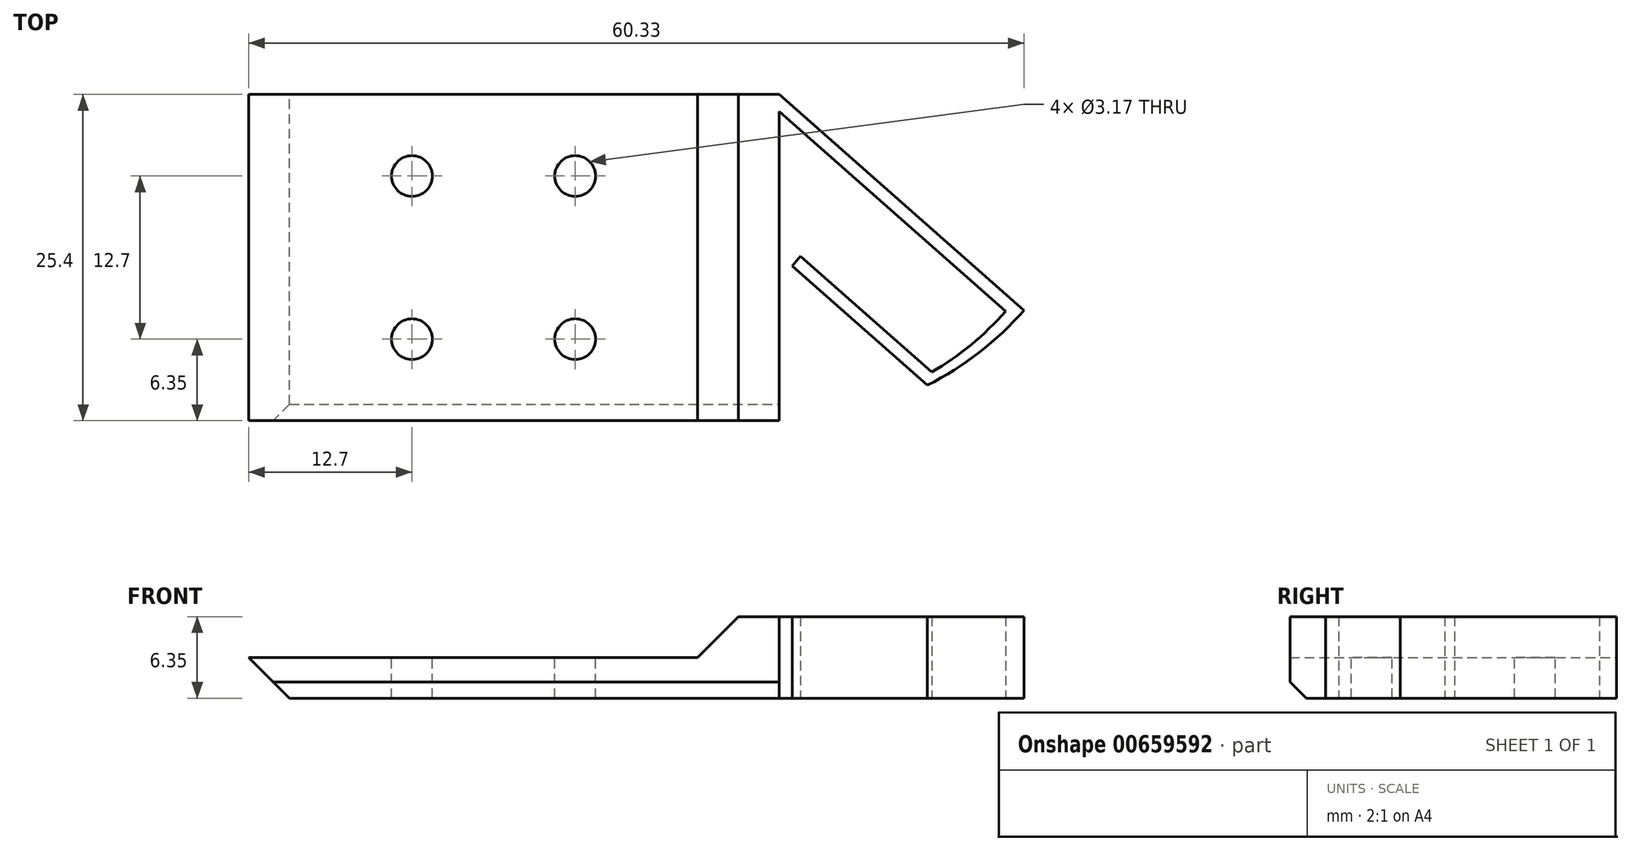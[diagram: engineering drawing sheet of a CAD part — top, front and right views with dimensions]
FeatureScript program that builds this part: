
annotation { "Feature Type Name" : "Feature", "Feature Type Description" : "" }
export const myFeature = defineFeature(function(context is Context, id is Id, definition is map)
    precondition{}
    {
        {
            var Q0;
            Q0=qCreatedBy(makeId("Top.planeOp"),FACE);
            var sketch = newSketch(context, id + "F0", { "sketchPlane" : qUnion([Q0])});
            skLineSegment(sketch, "E0.bottom", {"start": v(28.58, -12.7) * mm, "end": v(-28.58, -12.7) * mm});
            skLineSegment(sketch, "E0.top", {"start": v(28.58, 12.7) * mm, "end": v(-28.58, 12.7) * mm});
            skLineSegment(sketch, "E0.left", {"start": v(28.58, -12.7) * mm, "end": v(28.58, 12.7) * mm});
            skLineSegment(sketch, "E0.right", {"start": v(-28.57, -12.7) * mm, "end": v(-28.57, 12.7) * mm});
            skPoint(sketch, "E0.middle", {"position": v(0, 0) * mm});
            skLineSegment(sketch, "E1", {"start": v(-9.53, 11.37) * mm, "end": v(-9.52, -12.7) * mm});
            skLineSegment(sketch, "E2", {"start": v(0, -12.7) * mm, "end": v(0, 12.7) * mm});
            skPoint(sketch, "E3", {"position": v(-22.22, -12.7) * mm});
            skLineSegment(sketch, "E4", {"start": v(-9.53, 12.7) * mm, "end": v(-28.57, -4.1) * mm});
            skPoint(sketch, "E5", {"position": v(-19.05, -12.7) * mm});
            skArc(sketch, "E6", {"start": v(-28.57, -4.1) * mm, "mid": v(-25.09, -7.37) * mm, "end": v(-21.05, -9.94) * mm});
            skLineSegment(sketch, "E7", {"start": v(-21.05, -9.94) * mm, "end": v(-10.53, -0.66) * mm});
            skLineSegment(sketch, "E8", {"start": v(-10.53, -0.66) * mm, "end": v(-11.19, 0.1) * mm});
            skLineSegment(sketch, "E9", {"start": v(-11.19, 0.1) * mm, "end": v(-11.19, 0.1) * mm});
            skLineSegment(sketch, "E10", {"start": v(-9.53, 11.37) * mm, "end": v(-27.15, -4.18) * mm});
            skArc(sketch, "E11", {"start": v(-27.15, -4.18) * mm, "mid": v(-24.46, -6.77) * mm, "end": v(-21.4, -8.91) * mm});
            skLineSegment(sketch, "E12", {"start": v(-21.4, -8.91) * mm, "end": v(-11.19, 0.1) * mm});
            skSolve(sketch);
        }
        {
            var Q0;
            {var subQ0=sQuery(id+"F0.wireOp",EDGE,"E0.left");Q0=makeQuery(id+"F0.imprint","IMPRINT",FACE,{"disambiguationData":[TD([[makeQuery(id+"F0.imprint","IMPRINT",EDGE,{"derivedFrom":subQ0}),1.0]])]});}
            var Q1;
            {var subQ1=sQuery(id+"F0.wireOp",EDGE,"E1");Q1=makeQuery(id+"F0.imprint","IMPRINT",FACE,{"disambiguationData":[TD([[makeQuery(id+"F0.imprint","IMPRINT",EDGE,{"derivedFrom":subQ1}),1.0]])]});}
            var Q2;
            {var subQ0=sQuery(id+"F0.wireOp",EDGE,"Ll8NUgnO-918t-zldm-zNWz-RsUZQomu35K8");Q2=makeQuery(id+"F0.imprint","IMPRINT",FACE,{"disambiguationData":[TD([[makeQuery(id+"F0.imprint","IMPRINT",EDGE,{"derivedFrom":subQ0}),1.0]])]});}
            extrude(context, id + "F1", {"entities" : qUnion([Q0, Q1, Q2]), "depth" : 3.17 * mm, "offsetDistance" : 25.4 * mm});
        }
        {
            var Q0;
            {var subQ1=sQuery(id+"F0.wireOp",EDGE,"E1");Q0=makeQuery(id+"F0.imprint","IMPRINT",FACE,{"disambiguationData":[TD([[makeQuery(id+"F0.imprint","IMPRINT",EDGE,{"derivedFrom":subQ1}),1.0]])]});}
            extrude(context, id + "F2", {"entities" : qUnion([Q0]), "operationType" : NewBodyOperationType.ADD, "depth" : 6.35 * mm, "offsetDistance" : 25.4 * mm});
        }
        {
            var Q0;
            Q0=makeQuery(id+"F2.opExtrude","CAP_EDGE",EDGE,{"disambiguationData":[OSD([sQuery(id+"F0.wireOp",EDGE,"E2")])],"isStart":false});
            chamfer(context, id + "F3", {"entities" : qUnion([Q0]), "width" : 6.35 * mm, "tangentPropagation" : true});
        }
        {
            var Q0;
            {var subQ0=sQuery(id+"F0.wireOp",EDGE,"E0.left");Q0=makeQuery(id+"F37SAEC6IVc2ddh_1.boolean.opBoolean","MERGE",FACE,{"derivedFrom":[makeQuery(id+"F1.opExtrude","SWEPT_FACE",FACE,{"disambiguationData":[OSD([subQ0])]}),makeQuery(id+"F37SAEC6IVc2ddh_1.opExtrude","SWEPT_FACE",FACE,{"disambiguationData":[OSD([subQ0])]})]});}
            cPlane(context, id + "F4", {"entities" : qUnion([Q0]), "cplaneType" : CPlaneType.OFFSET, "offset" : 3.17 * mm, "width" : 152.4 * mm, "height" : 152.4 * mm});
        }
        {
            var Q0;
            {var subQ0=sQuery(id+"F0.wireOp",EDGE,"E1");Q0=makeQuery(id+"F2.boolean.opBoolean","MERGE",FACE,{"derivedFrom":[makeQuery(id+"F1.opExtrude","SWEPT_FACE",FACE,{"disambiguationData":[OSD([subQ0])]}),makeQuery(id+"F2.opExtrude","SWEPT_FACE",FACE,{"disambiguationData":[OSD([subQ0])]})]});}
            var sketch = newSketch(context, id + "F5", { "sketchPlane" : qUnion([Q0])});
            skLineSegment(sketch, "E13", {"start": v(12.7, 0) * mm, "end": v(12.7, 1.27) * mm});
            skLineSegment(sketch, "E14", {"start": v(12.7, 1.27) * mm, "end": v(11.43, 0) * mm});
            skLineSegment(sketch, "E15", {"start": v(11.43, 0) * mm, "end": v(12.7, 0) * mm});
            skSolve(sketch);
        }
        {
            var Q0;
            {var subQ0=sQuery(id+"F0.wireOp",EDGE,"E0.top");Q0=makeQuery(id+"F2.boolean.opBoolean","MERGE",FACE,{"derivedFrom":[makeQuery(id+"F1.opExtrude","SWEPT_FACE",FACE,{"disambiguationData":[OSD([subQ0])]}),makeQuery(id+"F2.opExtrude","SWEPT_FACE",FACE,{"disambiguationData":[OSD([subQ0])]})]});}
            var sketch = newSketch(context, id + "F6", { "sketchPlane" : qUnion([Q0])});
            skLineSegment(sketch, "E16", {"start": v(-28.58, 3.18) * mm, "end": v(-31.75, 3.18) * mm});
            skLineSegment(sketch, "E17", {"start": v(-31.75, 3.18) * mm, "end": v(-28.58, 0) * mm});
            skLineSegment(sketch, "E18", {"start": v(-28.58, 0) * mm, "end": v(-28.58, 3.18) * mm});
            skSolve(sketch);
        }
        {
            var Q0;
            Q0=makeQuery(id+"F6.imprint","IMPRINT",FACE,{"disambiguationData":[TD([[makeQuery(id+"F6.imprint","IMPRINT",EDGE,{"derivedFrom":sQuery(id+"F6.wireOp",EDGE,"E18")}),1.0]])]});
            var Q1;
            Q1=makeQuery(id+"F6.imprint","IMPRINT",FACE,{"disambiguationData":[TD([[makeQuery(id+"F6.imprint","IMPRINT",EDGE,{"derivedFrom":sQuery(id+"F6.wireOp",EDGE,"E16")}),1.0]])]});
            extrude(context, id + "F7", {"entities" : qUnion([Q0, Q1]), "operationType" : NewBodyOperationType.ADD, "oppositeDirection" : true, "depth" : 25.4 * mm, "offsetDistance" : 25.4 * mm});
        }
        {
            var Q0;
            Q0=makeQuery(id+"F5.imprint","IMPRINT",FACE,{"disambiguationData":[TD([[makeQuery(id+"F5.imprint","IMPRINT",EDGE,{"derivedFrom":sQuery(id+"F5.wireOp",EDGE,"E13")}),-1.0]])]});
            extrude(context, id + "F8", {"entities" : qUnion([Q0]), "operationType" : NewBodyOperationType.REMOVE, "oppositeDirection" : true, "depth" : 50.8 * mm, "offsetDistance" : 25.4 * mm});
        }
        {
            var Q0;
            Q0=makeQuery(id+"F1.opExtrude","SWEPT_BODY",BODY,{"disambiguationData":[OSD([sQuery(id+"F0.wireOp",EDGE,"E0.bottom"),sQuery(id+"F0.wireOp",EDGE,"E0.top"),sQuery(id+"F0.wireOp",EDGE,"E0.left"),sQuery(id+"F0.wireOp",EDGE,"E1"),sQuery(id+"F0.wireOp",EDGE,"E4"),sQuery(id+"F0.wireOp",EDGE,"E6"),sQuery(id+"F0.wireOp",EDGE,"E7"),sQuery(id+"F0.wireOp",EDGE,"E8"),sQuery(id+"F0.wireOp",EDGE,"E10"),sQuery(id+"F0.wireOp",EDGE,"E11"),sQuery(id+"F0.wireOp",EDGE,"E12")])]});
            var Q1;
            Q1=qCreatedBy(id+"F4.planeOp",FACE);
            mirror(context, id + "F9", {"entities" : qUnion([Q0]), "mirrorPlane" : qUnion([Q1])});
        }
        {
            var Q0;
            {var subQ0=sQuery(id+"F0.wireOp",EDGE,"E0.top");Q0=makeQuery(id+"F7.boolean.opBoolean","MERGE",FACE,{"derivedFrom":[makeQuery(id+"F1.opExtrude","CAP_FACE",FACE,{"disambiguationData":[OSD([sQuery(id+"F0.wireOp",EDGE,"E0.bottom"),subQ0,sQuery(id+"F0.wireOp",EDGE,"E0.left"),sQuery(id+"F0.wireOp",EDGE,"E1"),sQuery(id+"F0.wireOp",EDGE,"E4"),sQuery(id+"F0.wireOp",EDGE,"E6"),sQuery(id+"F0.wireOp",EDGE,"E7"),sQuery(id+"F0.wireOp",EDGE,"E8"),sQuery(id+"F0.wireOp",EDGE,"E10"),sQuery(id+"F0.wireOp",EDGE,"E11"),sQuery(id+"F0.wireOp",EDGE,"E12")])],"isStart":false}),makeQuery(id+"F7.opExtrude","SWEPT_FACE",FACE,{"disambiguationData":[OSD([subQ0,sQuery(id+"F6.wireOp",EDGE,"E16")])]})]});}
            var sketch = newSketch(context, id + "F10", { "sketchPlane" : qUnion([Q0])});
            skLineSegment(sketch, "E19", {"start": v(31.75, 0) * mm, "end": v(19.05, 0) * mm, "construction": true});
            skPoint(sketch, "E19.endSnap0", {"position": v(-3.17, 0) * mm});
            skLineSegment(sketch, "E20", {"start": v(19.05, 0) * mm, "end": v(6.35, 0) * mm, "construction": true});
            skLineSegment(sketch, "E21", {"start": v(6.35, 0) * mm, "end": v(6.35, 0) * mm});
            skLineSegment(sketch, "E22", {"start": v(31.75, 0) * mm, "end": v(44.45, 0) * mm, "construction": true});
            skLineSegment(sketch, "E23", {"start": v(44.45, 0) * mm, "end": v(57.15, 0) * mm, "construction": true});
            skLineSegment(sketch, "E24.bottom", {"start": v(44.45, 6.35) * mm, "end": v(19.05, 6.35) * mm, "construction": true});
            skLineSegment(sketch, "E24.top", {"start": v(44.45, -6.35) * mm, "end": v(19.05, -6.35) * mm, "construction": true});
            skLineSegment(sketch, "E24.left", {"start": v(44.45, 6.35) * mm, "end": v(44.45, -6.35) * mm, "construction": true});
            skLineSegment(sketch, "E24.right", {"start": v(19.05, 6.35) * mm, "end": v(19.05, -6.35) * mm, "construction": true});
            skPoint(sketch, "E24.middle", {"position": v(31.75, 0) * mm});
            skLineSegment(sketch, "E25.bottom", {"start": v(57.15, 6.35) * mm, "end": v(6.35, 6.35) * mm, "construction": true});
            skLineSegment(sketch, "E25.top", {"start": v(57.15, -6.35) * mm, "end": v(6.35, -6.35) * mm, "construction": true});
            skLineSegment(sketch, "E25.left", {"start": v(57.15, 6.35) * mm, "end": v(57.15, -6.35) * mm, "construction": true});
            skLineSegment(sketch, "E25.right", {"start": v(6.35, 6.35) * mm, "end": v(6.35, -6.35) * mm, "construction": true});
            skSolve(sketch);
        }
        {
            var Q0;
            Q0=sQuery(id+"F10.wireOp",VERTEX,"E25.left.end");
            var Q1;
            Q1=sQuery(id+"F10.wireOp",VERTEX,"E25.bottom.start");
            var Q2;
            Q2=sQuery(id+"F10.wireOp",VERTEX,"E24.bottom.end");
            var Q3;
            Q3=sQuery(id+"F10.wireOp",VERTEX,"E24.right.end");
            var Q4;
            Q4=sQuery(id+"F10.wireOp",VERTEX,"E25.right.end");
            var Q5;
            Q5=sQuery(id+"F10.wireOp",VERTEX,"E25.bottom.end");
            var Q6;
            Q6=sQuery(id+"F10.wireOp",VERTEX,"E24.top.start");
            var Q7;
            Q7=sQuery(id+"F10.wireOp",VERTEX,"E24.bottom.start");
            var Q8;
            Q8=makeQuery(id+"F1.opExtrude","SWEPT_BODY",BODY,{"disambiguationData":[OSD([sQuery(id+"F0.wireOp",EDGE,"E0.bottom"),sQuery(id+"F0.wireOp",EDGE,"E0.top"),sQuery(id+"F0.wireOp",EDGE,"E0.left"),sQuery(id+"F0.wireOp",EDGE,"E1"),sQuery(id+"F0.wireOp",EDGE,"E4"),sQuery(id+"F0.wireOp",EDGE,"E6"),sQuery(id+"F0.wireOp",EDGE,"E7"),sQuery(id+"F0.wireOp",EDGE,"E8"),sQuery(id+"F0.wireOp",EDGE,"E10"),sQuery(id+"F0.wireOp",EDGE,"E11"),sQuery(id+"F0.wireOp",EDGE,"E12")])]});
            var Q9;
            Q9=makeQuery(id+"F9.opPattern","COPY",BODY,{"derivedFrom":makeQuery(id+"F1.opExtrude","SWEPT_BODY",BODY,{"disambiguationData":[OSD([sQuery(id+"F0.wireOp",EDGE,"E0.bottom"),sQuery(id+"F0.wireOp",EDGE,"E0.top"),sQuery(id+"F0.wireOp",EDGE,"E0.left"),sQuery(id+"F0.wireOp",EDGE,"E1"),sQuery(id+"F0.wireOp",EDGE,"E4"),sQuery(id+"F0.wireOp",EDGE,"E6"),sQuery(id+"F0.wireOp",EDGE,"E7"),sQuery(id+"F0.wireOp",EDGE,"E8"),sQuery(id+"F0.wireOp",EDGE,"E10"),sQuery(id+"F0.wireOp",EDGE,"E11"),sQuery(id+"F0.wireOp",EDGE,"E12")])]}),"instanceName":"1"});
            hole(context, id + "F11", {"style" : HoleStyle.SIMPLE, "endStyle" : HoleEndStyle.THROUGH, "holeDiameter" : 3.17 * mm, "majorDiameter" : 6.35 * mm, "isTappedThrough" : true, "tappedDepth" : 12.7 * mm, "tapClearance" : 3, "locations" : qUnion([Q0, Q1, Q2, Q3, Q4, Q5, Q6, Q7]), "scope" : qUnion([Q8, Q9])});
        }
        {
            var Q0;
            Q0=makeQuery(id+"F1.opExtrude","SWEPT_BODY",BODY,{"disambiguationData":[OSD([sQuery(id+"F0.wireOp",EDGE,"E0.bottom"),sQuery(id+"F0.wireOp",EDGE,"E0.top"),sQuery(id+"F0.wireOp",EDGE,"E0.left"),sQuery(id+"F0.wireOp",EDGE,"E1"),sQuery(id+"F0.wireOp",EDGE,"E4"),sQuery(id+"F0.wireOp",EDGE,"E6"),sQuery(id+"F0.wireOp",EDGE,"E7"),sQuery(id+"F0.wireOp",EDGE,"E8"),sQuery(id+"F0.wireOp",EDGE,"E10"),sQuery(id+"F0.wireOp",EDGE,"E11"),sQuery(id+"F0.wireOp",EDGE,"E12")])]});
            deleteBodies(context, id + "F12", {"entities" : qUnion([Q0])});
        }
    });
